# Revit family: 2CKA006599A3017
name_source: partatom
category: Elektroinstallationen
revit_build: Autodesk Revit 2017 (Build: 20160225_1515(x64)
units: mm (PartAtom-declared; Revit-internal decimal feet)

## family parameters
Basisbauteil = Fläche
Beim Laden mit Abzugskörper schneiden = Nein
Bemaßung runder Anschluss = Durchmesser verwenden
Beschriftungsausrichtung beibehalten = Ja
Gemeinsam genutzt = Nein
Raumberechnungspunkt = Nein
Teiletyp = Normal

## types (1)
- 2CKA006599A3017
    Aufdruck/Kennzeichnung = ohne Aufdruck
    Ausführung = Drehknopf
    Ausführung der Oberfläche = glänzend
    BIM = https://media.live.bim.site
    BIMSITE_PRODUCT_ID = 00f30aae18db8cf73b910521410f0ff52e8d4e1d
    Befestigungsart = Schraubbefestigung
    Beschreibung = Zentralscheibe, alpinweiß, Busch-balance SI, Bedienelemente für Dimmer, Zentralscheibe mit Drehknopf, Bef.-Mutter und Glimmlampe Für Busch-Dimmer. Für Einsatz 2112 U-101/2247 U/2250 U/6513 U-102/6517 U-10x/6519 U/6520 U/6523 U(R)(10x) /6591 U-10x und 6592 U.
    Datenblatt = https://media.live.bim.site
    Farbe = weiß
    GTIN = 4011395190678
    Geeignet für Schutzart (IP) = IP20
    Gerätebreite [mm] = 55
    Gerätehöhe [mm] = 55
    Gerätetiefe [mm] = 11
    HAN = 2CKA006599A3017
    Halogenfrei = Ja
    HeinzeBIM = https://www.heinze.de
    Hersteller = Busch-Jaeger Elektro GmbH
    Indicator = Red
    Ist System = Nein
    Ist Zubehör = Nein
    Oberfläche = unbehandelt
    Produktseite = https://media.live.bim.site
    RAL-Nummer (ähnlich) = 9016
    TYPE = 2115-914
    Typname = Zentralscheibe, alpinweiß, Busch-balance SI, Bedienelemente für Dimmer
    Verwendung = Dimmer
    Vorgabe-Ansicht = 1219 mm
    Werkstoff = Kunststoff
    Werkstoffgüte = Thermoplast
    White = White

## geometry (parser evidence)
native form markers: Sweep x4
no freeform markers — native parametric forms only
